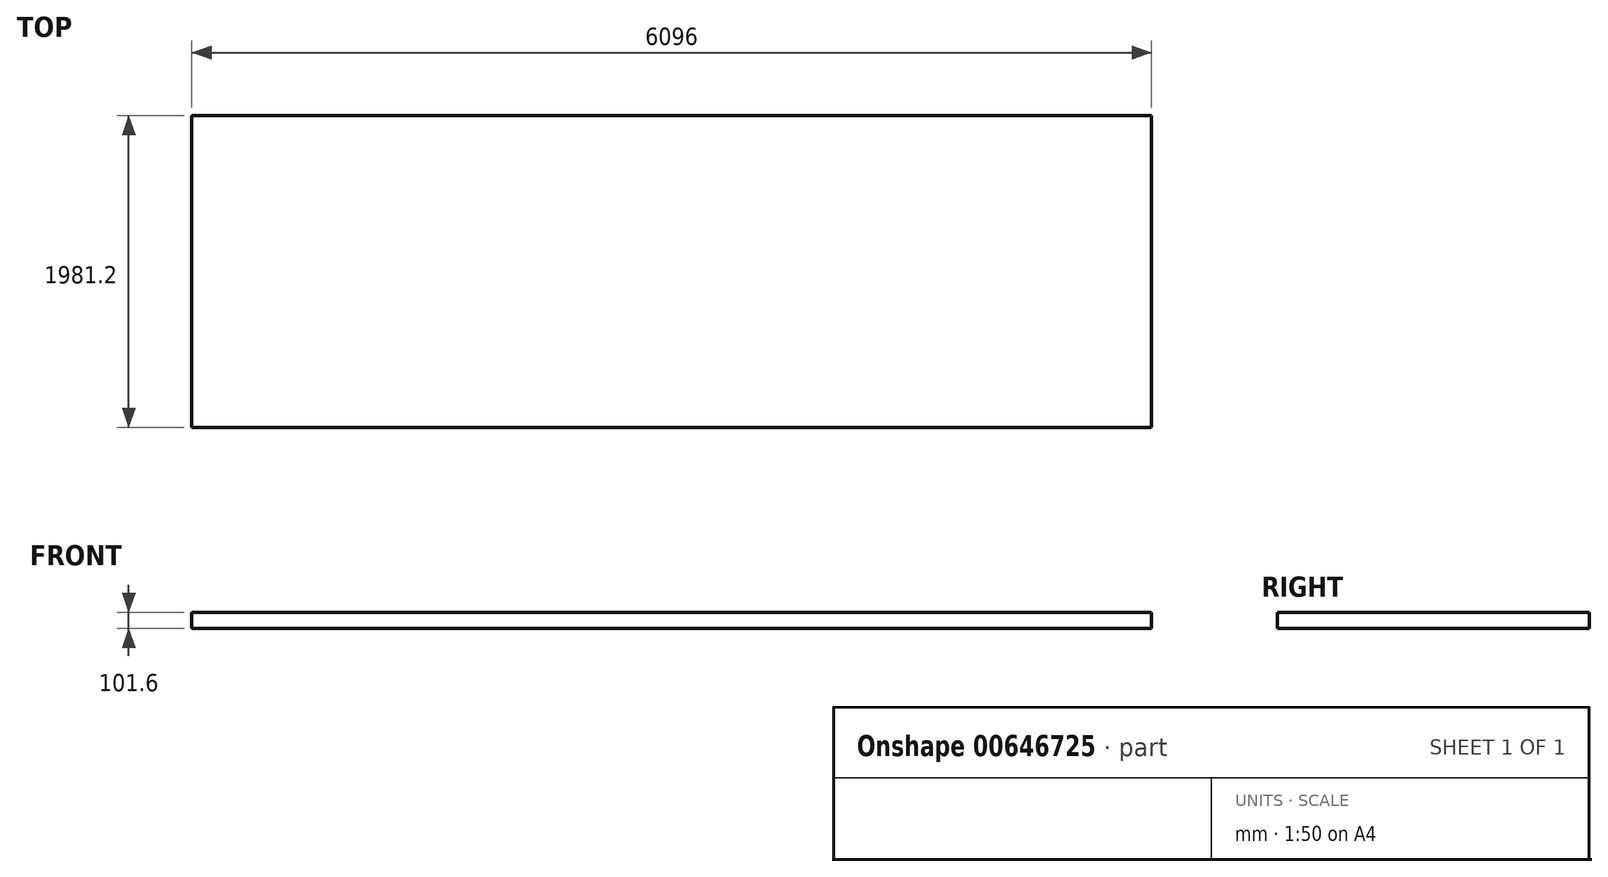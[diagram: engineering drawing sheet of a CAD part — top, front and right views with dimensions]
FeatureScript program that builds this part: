
annotation { "Feature Type Name" : "Feature", "Feature Type Description" : "" }
export const myFeature = defineFeature(function(context is Context, id is Id, definition is map)
    precondition{}
    {
        {
            var Q0;
            Q0=qCreatedBy(makeId("Top.planeOp"),FACE);
            var sketch = newSketch(context, id + "F0", { "sketchPlane" : qUnion([Q0])});
            skLineSegment(sketch, "E0.bottom", {"start": v(-947.46, 784.25) * mm, "end": v(5148.54, 784.25) * mm});
            skLineSegment(sketch, "E0.top", {"start": v(-947.46, -1196.95) * mm, "end": v(5148.54, -1196.95) * mm});
            skLineSegment(sketch, "E0.left", {"start": v(-947.46, 784.25) * mm, "end": v(-947.46, -1196.95) * mm});
            skLineSegment(sketch, "E0.right", {"start": v(5148.54, 784.25) * mm, "end": v(5148.54, -1196.95) * mm});
            skSolve(sketch);
        }
        {
            var Q0;
            Q0=makeQuery(id+"F0.imprint","IMPRINT",FACE,{"disambiguationData":[TD([[makeQuery(id+"F0.imprint","IMPRINT",EDGE,{"derivedFrom":sQuery(id+"F0.wireOp",EDGE,"E0.bottom")}),-1.0]])]});
            extrude(context, id + "F1", {"entities" : qUnion([Q0]), "depth" : 101.6 * mm, "offsetDistance" : 25.4 * mm});
        }
    });
